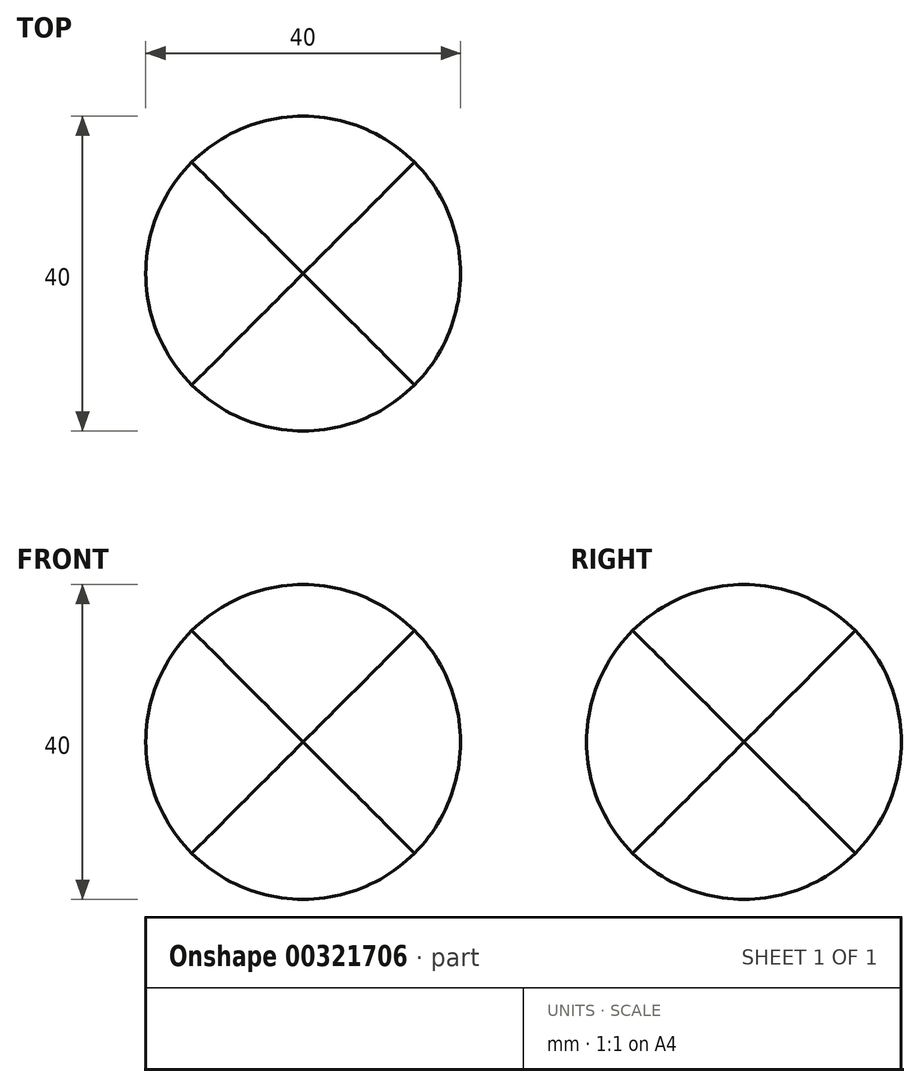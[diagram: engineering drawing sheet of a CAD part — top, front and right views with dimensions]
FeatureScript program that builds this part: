
annotation { "Feature Type Name" : "Feature", "Feature Type Description" : "" }
export const myFeature = defineFeature(function(context is Context, id is Id, definition is map)
    precondition{}
    {
        {
            var Q0;
            Q0=qCreatedBy(makeId("Front.planeOp"),FACE);
            var sketch = newSketch(context, id + "F0", { "sketchPlane" : qUnion([Q0])});
            skCircle(sketch, "E0", {"center": v(0, 0) * mm, "radius": 20 * mm});
            skSolve(sketch);
        }
        {
            var Q0;
            Q0 = qSketchRegion(id + "F0", true);
            extrude(context, id + "F1", {"entities" : qUnion([Q0]), "endBound" : BoundingType.SYMMETRIC, "depth" : 60 * mm});
        }
        {
            var Q0;
            Q0=qCreatedBy(makeId("Right.planeOp"),FACE);
            var Q1;
            Q1=qCreatedBy(makeId("Front.planeOp"),FACE);
            cPlane(context, id + "F2", {"entities" : qUnion([Q0, Q1]), "cplaneType" : CPlaneType.MID_PLANE, "offset" : 25 * mm, "width" : 150 * mm, "height" : 150 * mm});
        }
        {
            var Q0;
            Q0=qCreatedBy(id+"F2.planeOp",FACE);
            var sketch = newSketch(context, id + "F3", { "sketchPlane" : qUnion([Q0])});
            skLineSegment(sketch, "E1", {"start": v(0, 0) * mm, "end": v(-56.57, 40) * mm});
            skSolve(sketch);
        }
        {
            var Q0;
            Q0=makeQuery(id+"F1.opExtrude","SWEPT_BODY",BODY,{"disambiguationData":[OSD([sQuery(id+"F0.wireOp",EDGE,"E0")])]});
            var Q1;
            Q1=sQuery(id+"F3.wireOp",EDGE,"E1");
            circularPattern(context, id + "F4", {"entities" : qUnion([Q0]), "axis" : qUnion([Q1]), "angle" : 360 * degree, "instanceCount" : 3, "equalSpace" : true});
        }
        {
            var Q0;
            Q0=makeQuery(id+"F4.opPattern","COPY",BODY,{"derivedFrom":makeQuery(id+"F1.opExtrude","SWEPT_BODY",BODY,{"disambiguationData":[OSD([sQuery(id+"F0.wireOp",EDGE,"E0")])]}),"instanceName":"2"});
            var Q1;
            Q1=makeQuery(id+"F1.opExtrude","SWEPT_BODY",BODY,{"disambiguationData":[OSD([sQuery(id+"F0.wireOp",EDGE,"E0")])]});
            var Q2;
            Q2=makeQuery(id+"F4.opPattern","COPY",BODY,{"derivedFrom":makeQuery(id+"F1.opExtrude","SWEPT_BODY",BODY,{"disambiguationData":[OSD([sQuery(id+"F0.wireOp",EDGE,"E0")])]}),"instanceName":"1"});
            booleanBodies(context, id + "F5", {"operationType" : BooleanOperationType.INTERSECTION, "tools" : qUnion([Q0, Q1, Q2])});
        }
    });
